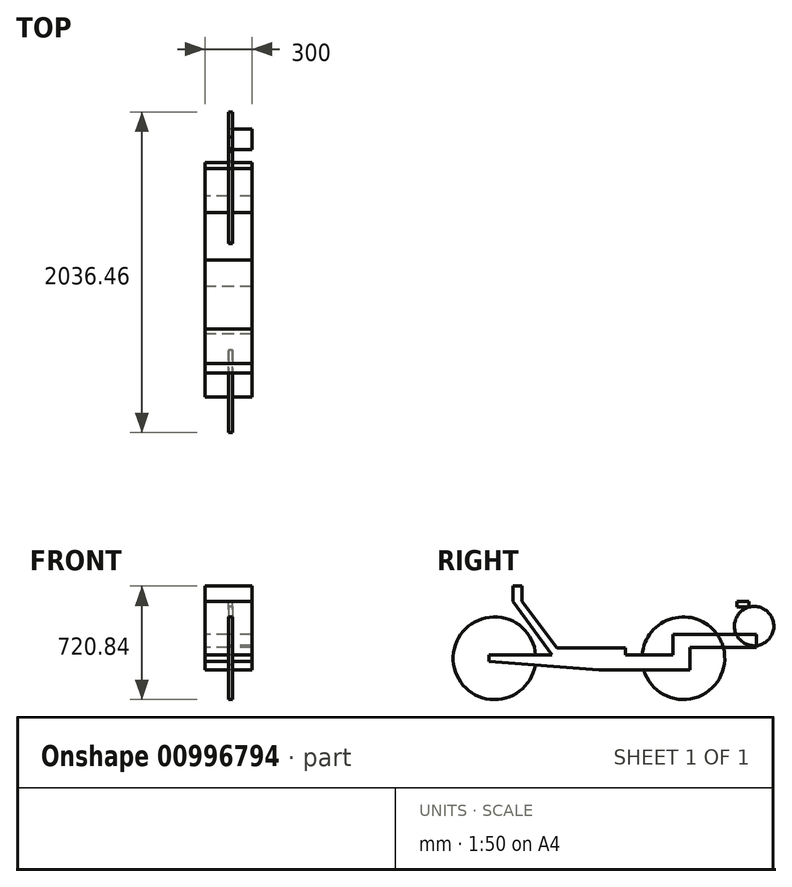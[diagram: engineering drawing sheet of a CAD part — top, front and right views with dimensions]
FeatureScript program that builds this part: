
annotation { "Feature Type Name" : "Feature", "Feature Type Description" : "" }
export const myFeature = defineFeature(function(context is Context, id is Id, definition is map)
    precondition{}
    {
        {
            var Q0;
            Q0=qCreatedBy(makeId("Right.planeOp"),FACE);
            var sketch = newSketch(context, id + "F0", { "sketchPlane" : qUnion([Q0])});
            skLineSegment(sketch, "E0", {"start": v(0, 0) * mm, "end": v(575.85, 0) * mm});
            skLineSegment(sketch, "E1", {"start": v(575.85, 0) * mm, "end": v(575.85, 142.06) * mm});
            skLineSegment(sketch, "E2", {"start": v(575.85, 142.06) * mm, "end": v(1000.7, 142.06) * mm});
            skLineSegment(sketch, "E3", {"start": v(1000.7, 142.06) * mm, "end": v(1000.7, 226.36) * mm});
            skLineSegment(sketch, "E4", {"start": v(1000.7, 226.36) * mm, "end": v(469.46, 226.36) * mm});
            skLineSegment(sketch, "E5", {"start": v(469.46, 226.36) * mm, "end": v(469.46, 94.81) * mm});
            skLineSegment(sketch, "E6", {"start": v(469.46, 94.81) * mm, "end": v(-699.3, 94.81) * mm});
            skLineSegment(sketch, "E7", {"start": v(-699.3, 94.81) * mm, "end": v(-699.3, 52.49) * mm});
            skLineSegment(sketch, "E8", {"start": v(-699.3, 52.49) * mm, "end": v(0, 0) * mm});
            skCircle(sketch, "E9", {"center": v(984.48, 277.8) * mm, "radius": 124.95 * mm});
            skCircle(sketch, "E10", {"center": v(-664.53, 73.65) * mm, "radius": 262.5 * mm});
            skPoint(sketch, "E10.centerSnap0", {"position": v(-699.3, 73.65) * mm});
            skCircle(sketch, "E11", {"center": v(535.47, 73.65) * mm, "radius": 262.5 * mm});
            skLineSegment(sketch, "E12", {"start": v(-301.04, 94.81) * mm, "end": v(-548.31, 435.55) * mm});
            skLineSegment(sketch, "E13", {"start": v(-548.31, 435.55) * mm, "end": v(-548.31, 531.99) * mm});
            skLineSegment(sketch, "E14", {"start": v(-548.31, 531.99) * mm, "end": v(-488.97, 531.99) * mm});
            skLineSegment(sketch, "E15", {"start": v(-488.97, 531.99) * mm, "end": v(-488.97, 435.55) * mm});
            skLineSegment(sketch, "E16", {"start": v(-488.97, 435.55) * mm, "end": v(-268.9, 138.82) * mm});
            skLineSegment(sketch, "E17", {"start": v(-268.9, 138.82) * mm, "end": v(168.79, 138.82) * mm});
            skLineSegment(sketch, "E18", {"start": v(168.79, 138.82) * mm, "end": v(168.79, 94.81) * mm});
            skLineSegment(sketch, "E19.bottom", {"start": v(875.92, 398.2) * mm, "end": v(951.07, 398.2) * mm});
            skLineSegment(sketch, "E19.top", {"start": v(875.92, 433.86) * mm, "end": v(951.07, 433.86) * mm});
            skLineSegment(sketch, "E19.left", {"start": v(951.07, 398.2) * mm, "end": v(951.07, 433.86) * mm});
            skLineSegment(sketch, "E19.right", {"start": v(875.92, 398.2) * mm, "end": v(875.92, 433.86) * mm});
            skSolve(sketch);
        }
        {
            var Q0;
            {var subQ4=sQuery(id+"F0.wireOp",EDGE,"E8");var subQ9=sQuery(id+"F0.wireOp",EDGE,"E0");var subQ10=makeQuery(id+"F0.imprint","INTERSECT",VERTEX,{"derivedFrom":[subQ9,subQ4]});Q0=makeQuery(id+"F0.imprint","IMPRINT",FACE,{"disambiguationData":[TD([[makeQuery(id+"F0.imprint","IMPRINT",EDGE,{"disambiguationData":[TD([[subQ10,-1.0]])],"derivedFrom":subQ9}),1.0]])]});}
            var Q1;
            {var subQ5=sQuery(id+"F0.wireOp",EDGE,"E1");Q1=makeQuery(id+"F0.imprint","IMPRINT",FACE,{"disambiguationData":[TD([[makeQuery(id+"F0.imprint","IMPRINT",EDGE,{"derivedFrom":subQ5}),1.0]])]});}
            var Q2;
            {var subQ0=sQuery(id+"F0.wireOp",EDGE,"E12");Q2=makeQuery(id+"F0.imprint","IMPRINT",FACE,{"disambiguationData":[TD([[makeQuery(id+"F0.imprint","IMPRINT",EDGE,{"derivedFrom":subQ0}),-1.0]])]});}
            var Q3;
            {var subQ0=sQuery(id+"F0.wireOp",EDGE,"E7");Q3=makeQuery(id+"F0.imprint","IMPRINT",FACE,{"disambiguationData":[TD([[makeQuery(id+"F0.imprint","IMPRINT",EDGE,{"derivedFrom":subQ0}),1.0]])]});}
            var Q4;
            {var subQ0=sQuery(id+"F0.wireOp",EDGE,"E4");var subQ1=sQuery(id+"F0.wireOp",EDGE,"E3");var subQ2=makeQuery(id+"F0.imprint","INTERSECT",VERTEX,{"derivedFrom":[subQ1,subQ0]});Q4=makeQuery(id+"F0.imprint","IMPRINT",FACE,{"disambiguationData":[TD([[makeQuery(id+"F0.imprint","IMPRINT",EDGE,{"disambiguationData":[TD([[subQ2,1.0]])],"derivedFrom":subQ1}),1.0]])]});}
            var Q5;
            {var subQ0=sQuery(id+"F0.wireOp",EDGE,"E11");var subQ1=sQuery(id+"F0.wireOp",EDGE,"E4");var subQ2=makeQuery(id+"F0.imprint","INTERSECT",VERTEX,{"derivedFrom":[subQ1,subQ0]});Q5=makeQuery(id+"F0.imprint","IMPRINT",FACE,{"disambiguationData":[TD([[makeQuery(id+"F0.imprint","IMPRINT",EDGE,{"disambiguationData":[TD([[subQ2,-1.0]])],"derivedFrom":subQ1}),1.0]])]});}
            extrude(context, id + "F1", {"entities" : qUnion([Q0, Q1, Q2, Q3, Q4, Q5]), "endBound" : BoundingType.SYMMETRIC, "depth" : 300 * mm, "offsetDistance" : 25 * mm});
        }
        {
            var Q0;
            Q0 = qSketchRegion(id + "F0", true);
            extrude(context, id + "F2", {"entities" : qUnion([Q0]), "operationType" : NewBodyOperationType.ADD, "depth" : 25 * mm, "offsetDistance" : 25 * mm});
        }
        {
            var Q0;
            {var subQ0=sQuery(id+"F0.wireOp",EDGE,"E4");Q0=makeQuery(id+"F1.opExtrude","SWEPT_FACE",FACE,{"disambiguationData":[OSD([subQ0]),TDD([makeQuery(id+"F0.imprint","IMPRINT",EDGE,{"disambiguationData":[TD([[makeQuery(id+"F0.imprint","INTERSECT",VERTEX,{"derivedFrom":[sQuery(id+"F0.wireOp",EDGE,"E3"),subQ0]}),-1.0]])],"derivedFrom":subQ0})])]});}
            var sketch = newSketch(context, id + "F3", { "sketchPlane" : qUnion([Q0])});
            skLineSegment(sketch, "E20.bottom", {"start": v(-150, 1000.7) * mm, "end": v(0, 1000.7) * mm});
            skLineSegment(sketch, "E20.top", {"start": v(-150, 870.6) * mm, "end": v(0, 870.6) * mm});
            skLineSegment(sketch, "E20.left", {"start": v(-150, 1000.7) * mm, "end": v(-150, 870.6) * mm});
            skLineSegment(sketch, "E20.right", {"start": v(0, 1000.7) * mm, "end": v(0, 870.6) * mm});
            skLineSegment(sketch, "E21.bottom", {"start": v(150, 870.6) * mm, "end": v(25.77, 870.6) * mm});
            skLineSegment(sketch, "E21.left", {"start": v(150, 870.6) * mm, "end": v(150, 1000.7) * mm});
            skLineSegment(sketch, "E21.right", {"start": v(25.77, 870.6) * mm, "end": v(25.77, 1000.7) * mm});
            skSolve(sketch);
        }
        {
            var Q0;
            Q0 = qSketchRegion(id + "F3", true);
            var Q1;
            Q1=makeQuery(id+"F3.imprint","IMPRINT",FACE,{"disambiguationData":[TD([[makeQuery(id+"F3.imprint","IMPRINT",EDGE,{"derivedFrom":sQuery(id+"F3.wireOp",EDGE,"E21.bottom")}),-1.0]])]});
            extrude(context, id + "F4", {"entities" : qUnion([Q0, Q1]), "operationType" : NewBodyOperationType.REMOVE, "oppositeDirection" : true, "depth" : 150 * mm, "offsetDistance" : 25 * mm});
        }
    });
